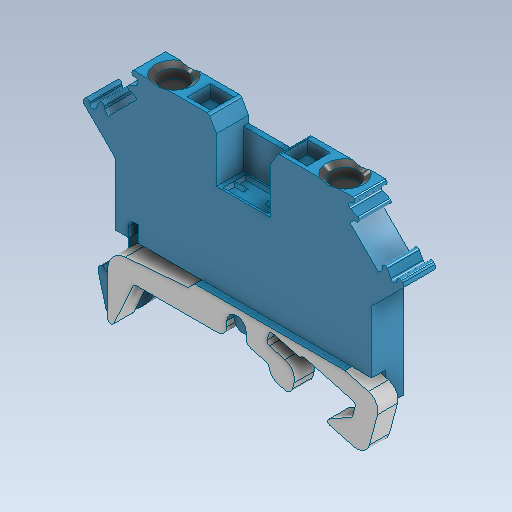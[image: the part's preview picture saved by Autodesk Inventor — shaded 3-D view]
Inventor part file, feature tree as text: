
AUTODESK INVENTOR PART (.ipt)
format: ipt  version: 2025.2 (Build 292293000, 293)  size: 826,880 bytes
history: native  units: mm
features: other x130, sketch x12, extrude x10, hole x2
ambient origin geometry x8: Origin, YZ Plane, XZ Plane, XY Plane, X Axis, Y Axis, Z Axis, Center Point
bodies: Solid1 (feature_tree)
feature tree (154):
  extrude  "Extrusion1"  Depth=2.1mm TaperAngle=0.0deg
  extrude  "Extrusion2"  Depth=2.0mm TaperAngle=0.0deg
  extrude  "Extrusion3"  Depth=7.0mm TaperAngle=0.0deg
  extrude  "Extrusion4"  Depth=5.0mm TaperAngle=0.0deg
  extrude  "Extrusion5"  Depth=3.6mm TaperAngle=0.0deg
  extrude  "Extrusion6"  TaperAngle=0.0deg  [1 undecoded]
  extrude  "Extrusion7"  TaperAngle=0.0deg  [1 undecoded]
  extrude  "Extrusion8"  TaperAngle=0.0deg  [1 undecoded]
  hole  "Hole1"  [1 undecoded]
  hole  "Hole2"  [1 undecoded]
  extrude  "Extrusion9"  Depth=10.0mm
  extrude  "Extrusion10"  Depth=10.0mm
  other  "1_2_XY"
  other  "1_2_YZ"
  other  "1_2_ZX"
  other  "1_2_X"
  other  "1_2_Y"
  other  "1_2_Z"
  other  "1_2_Center"
  other  "1_3_XY"
  other  "1_3_YZ"
  other  "1_3_ZX"
  other  "1_3_X"
  other  "1_3_Y"
  other  "1_3_Z"
  other  "1_3_Center"
  other  "1_4_XY"
  other  "1_4_YZ"
  other  "1_4_ZX"
  other  "1_4_X"
  other  "1_4_Y"
  other  "1_4_Z"
  other  "1_4_Center"
  other  "1_5_XY"
  other  "1_5_YZ"
  other  "1_5_ZX"
  other  "1_5_X"
  other  "1_5_Y"
  other  "1_5_Z"
  other  "1_5_Center"
  other  "1_6_XY"
  other  "1_6_YZ"
  other  "1_6_ZX"
  other  "1_6_X"
  other  "1_6_Y"
  other  "1_6_Z"
  other  "1_6_Center"
  other  "1_7_XY"
  other  "1_7_YZ"
  other  "1_7_ZX"
  other  "1_7_X"
  other  "1_7_Y"
  other  "1_7_Z"
  other  "1_7_Center"
  other  "1_8_XY"
  other  "1_8_YZ"
  other  "1_8_ZX"
  other  "1_8_X"
  other  "1_8_Y"
  other  "1_8_Z"
  other  "1_8_Center"
  other  "MD_XY"
  other  "MD_YZ"
  other  "MD_ZX"
  other  "MD_X"
  other  "MD_Y"
  other  "MD_Z"
  other  "MD_Center"
  other  "OP_XY"
  other  "OP_YZ"
  other  "OP_ZX"
  other  "OP_X"
  other  "OP_Y"
  other  "OP_Z"
  other  "OP_Center"
  other  "a1_XY"
  other  "a1_YZ"
  other  "a1_ZX"
  other  "a1_X"
  other  "a1_Y"
  other  "a1_Z"
  other  "a1_Center"
  other  "b2_XY"
  other  "b2_YZ"
  other  "b2_ZX"
  other  "b2_X"
  other  "b2_Y"
  other  "b2_Z"
  other  "b2_Center"
  other  "j3_XY"
  other  "j3_YZ"
  other  "j3_ZX"
  other  "j3_X"
  other  "j3_Y"
  other  "j3_Z"
  other  "j3_Center"
  other  "m4_XY"
  other  "m4_YZ"
  other  "m4_ZX"
  other  "m4_X"
  other  "m4_Y"
  other  "m4_Z"
  other  "m4_Center"
  other  "m5_XY"
  other  "m5_YZ"
  other  "m5_ZX"
  other  "m5_X"
  other  "m5_Y"
  other  "m5_Z"
  other  "m5_Center"
  other  "z6_XY"
  other  "z6_YZ"
  other  "z6_ZX"
  other  "z6_X"
  other  "z6_Y"
  other  "z6_Z"
  other  "z6_Center"
  other  "z7_XY"
  other  "z7_YZ"
  other  "z7_ZX"
  other  "z7_X"
  other  "z7_Y"
  other  "z7_Z"
  other  "z7_Center"
  other  "Edição direta1"
  other  "Edição direta2"
  other  "Edição direta3"
  other  "Edição direta4"
  other  "Edição direta5"
  other  "Edição direta6"
  other  "Edição direta7"
  other  "Edição direta8"
  other  "Edição direta9"
  sketch  "Skizze_1"  dims[d0=5.0mm d1=0.0mm d2=2.1mm d3=0.0mm]
  sketch  "Skizze_14"  dims[d39=0.0mm d40=0.0mm]
  sketch  "Skizze_15"  dims[d41=3.0mm d42=10.0mm d43=10.0mm d44=12.3mm d45=10.0mm d46=10.0mm]
  sketch  "Skizze_16"  dims[d47=12.0mm d48=10.0mm d49=10.0mm d50=0.25mm d51=0.55mm d52=-0.36mm d53=-0.4mm d54=0.0mm d55=0.0mm d56=0.0mm d57=0.0mm d58=0.35mm d59=0.5mm]
  sketch  "Skizze_2"  dims[d4=2.1mm d5=0.0mm d6=2.0mm d7=0.0mm]
  sketch  "Skizze_3"  dims[d8=0.8mm d9=0.0mm d10=7.0mm d11=0.0mm]
  sketch  "Skizze_4"  dims[d12=3.4mm d13=0.0mm d14=5.0mm d15=0.0mm]
  sketch  "Skizze_5"  dims[d16=4.2mm d17=6.0mm d18=5.8mm d19=2.0mm d20=18.545904mm d21=2.0mm d22=0.0mm]
  sketch  "Sketch9"  dims[d32=3.6mm d33=0.0mm d34=0.0mm]
  sketch  "Sketch10"  dims[d37=0.0mm d38=0.0mm]
  sketch  "Skizze_8"  dims[d23=4.2mm d24=6.0mm d25=5.8mm d26=2.0mm d27=18.545904mm d28=2.0mm d29=0.0mm d30=3.6mm d31=0.0mm]
  sketch  "Skizze_9"  dims[d35=0.0mm d36=0.0mm]
  other  "Escala1"
  other  "Escala2"
  other  "Escala3"
  other  "Tamanho1"
  other  "Tamanho2"
  other  "Tamanho3"
  other  "Mover1"
  other  "Mover2"
  other  "Tamanho4"
note: 5 required parameter values undecoded (feature->parameter linkage not recoverable at this tier; creation-order binding heuristic only, values carry confidence <= 0.55)
